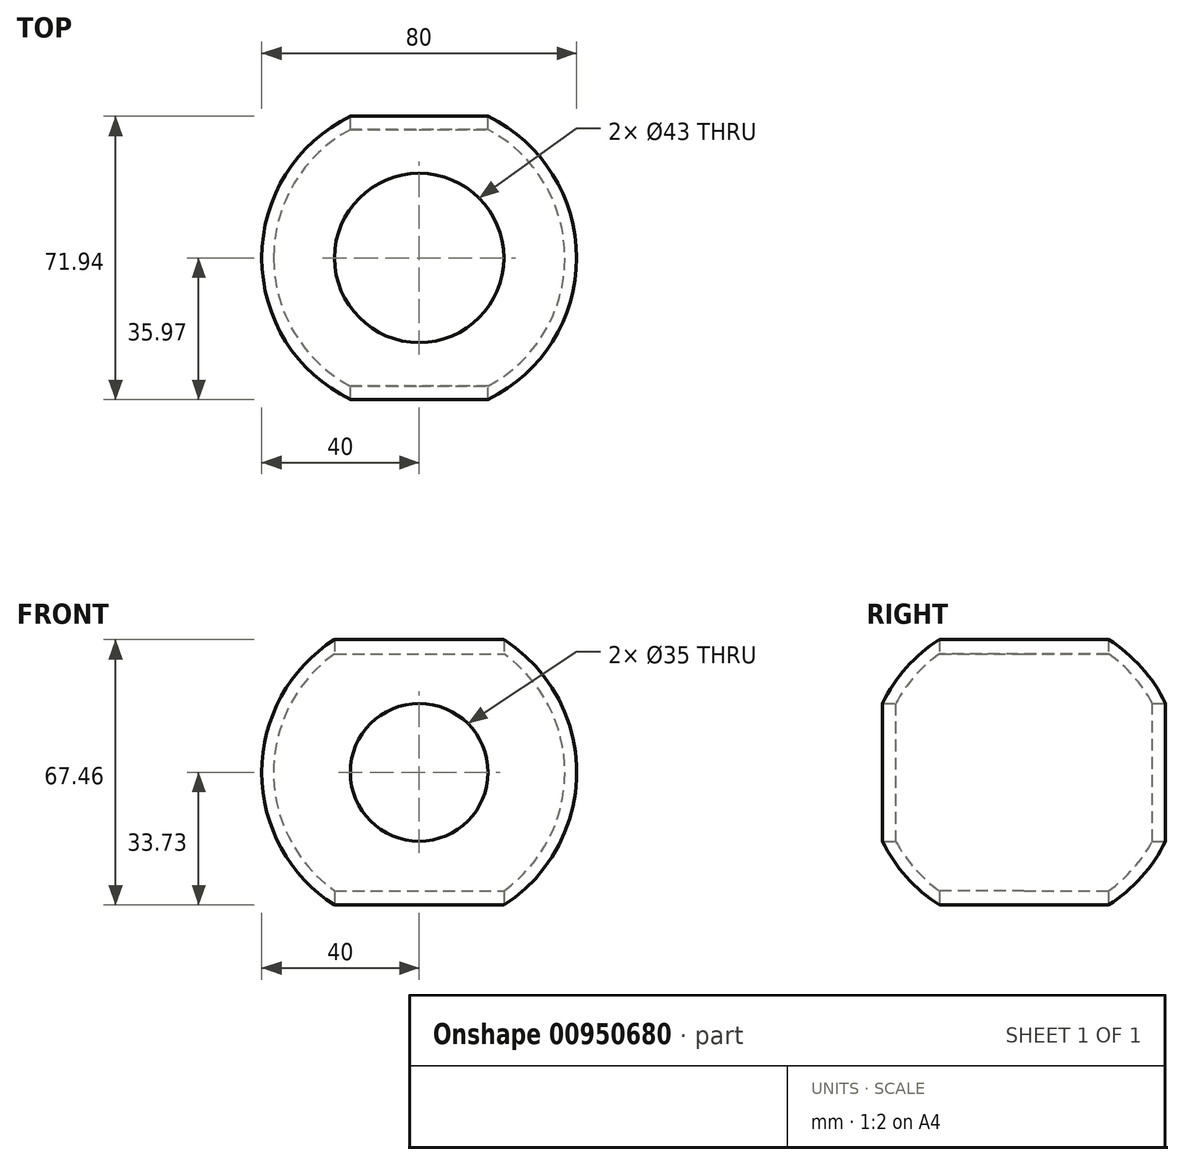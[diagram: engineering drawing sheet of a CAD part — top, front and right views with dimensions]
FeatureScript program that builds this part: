
annotation { "Feature Type Name" : "Feature", "Feature Type Description" : "" }
export const myFeature = defineFeature(function(context is Context, id is Id, definition is map)
    precondition{}
    {
        {
            var Q0;
            Q0=qCreatedBy(makeId("Front.planeOp"),FACE);
            var sketch = newSketch(context, id + "F0", { "sketchPlane" : qUnion([Q0])});
            skArc(sketch, "E0", {"start": v(0, 40) * mm, "mid": v(-40, 0) * mm, "end": v(0, -40) * mm});
            skArc(sketch, "E1", {"start": v(0, 37) * mm, "mid": v(-37, 0) * mm, "end": v(0, -37) * mm});
            skLineSegment(sketch, "E2", {"start": v(0, 37) * mm, "end": v(0, 40) * mm});
            skLineSegment(sketch, "E3", {"start": v(0, -37) * mm, "end": v(0, -40) * mm});
            skSolve(sketch);
        }
        {
            var Q0;
            Q0=makeQuery(id+"F0.imprint","IMPRINT",FACE,{"disambiguationData":[TD([[makeQuery(id+"F0.imprint","IMPRINT",EDGE,{"derivedFrom":sQuery(id+"F0.wireOp",EDGE,"E0")}),1.0]])]});
            var Q1;
            Q1=sQuery(id+"F0.wireOp",EDGE,"E3");
            revolve(context, id + "F1", {"surfaceOperationType" : NewSurfaceOperationType.NEW, "entities" : qUnion([Q0]), "axis" : qUnion([Q1]), "revolveType" : RevolveType.FULL, "oppositeDirection" : true});
        }
        {
            var Q0;
            Q0=qCreatedBy(makeId("Front.planeOp"),FACE);
            var sketch = newSketch(context, id + "F2", { "sketchPlane" : qUnion([Q0])});
            skCircle(sketch, "E4", {"center": v(0, 0) * mm, "radius": 17.5 * mm});
            skSolve(sketch);
        }
        {
            var Q0;
            Q0=qSketchRegion(id+"F2",true);
            extrude(context, id + "F3", {"entities" : qUnion([Q0]), "operationType" : NewBodyOperationType.REMOVE, "endBound" : BoundingType.THROUGH_ALL, "depth" : 25 * mm, "offsetDistance" : 25 * mm, "hasSecondDirection" : true, "secondDirectionBound" : BoundingType.THROUGH_ALL, "secondDirectionOppositeDirection" : true, "secondDirectionDepth" : 25 * mm});
        }
        {
            var Q0;
            Q0=qCreatedBy(makeId("Top.planeOp"),FACE);
            var sketch = newSketch(context, id + "F4", { "sketchPlane" : qUnion([Q0])});
            skCircle(sketch, "E5", {"center": v(0, 0) * mm, "radius": 21.5 * mm});
            skSolve(sketch);
        }
        {
            var Q0;
            Q0 = qSketchRegion(id + "F4", true);
            extrude(context, id + "F5", {"entities" : qUnion([Q0]), "operationType" : NewBodyOperationType.REMOVE, "endBound" : BoundingType.THROUGH_ALL, "depth" : 25 * mm, "offsetDistance" : 25 * mm, "hasSecondDirection" : true, "secondDirectionBound" : BoundingType.THROUGH_ALL, "secondDirectionOppositeDirection" : true, "secondDirectionDepth" : 25 * mm});
        }
    });
